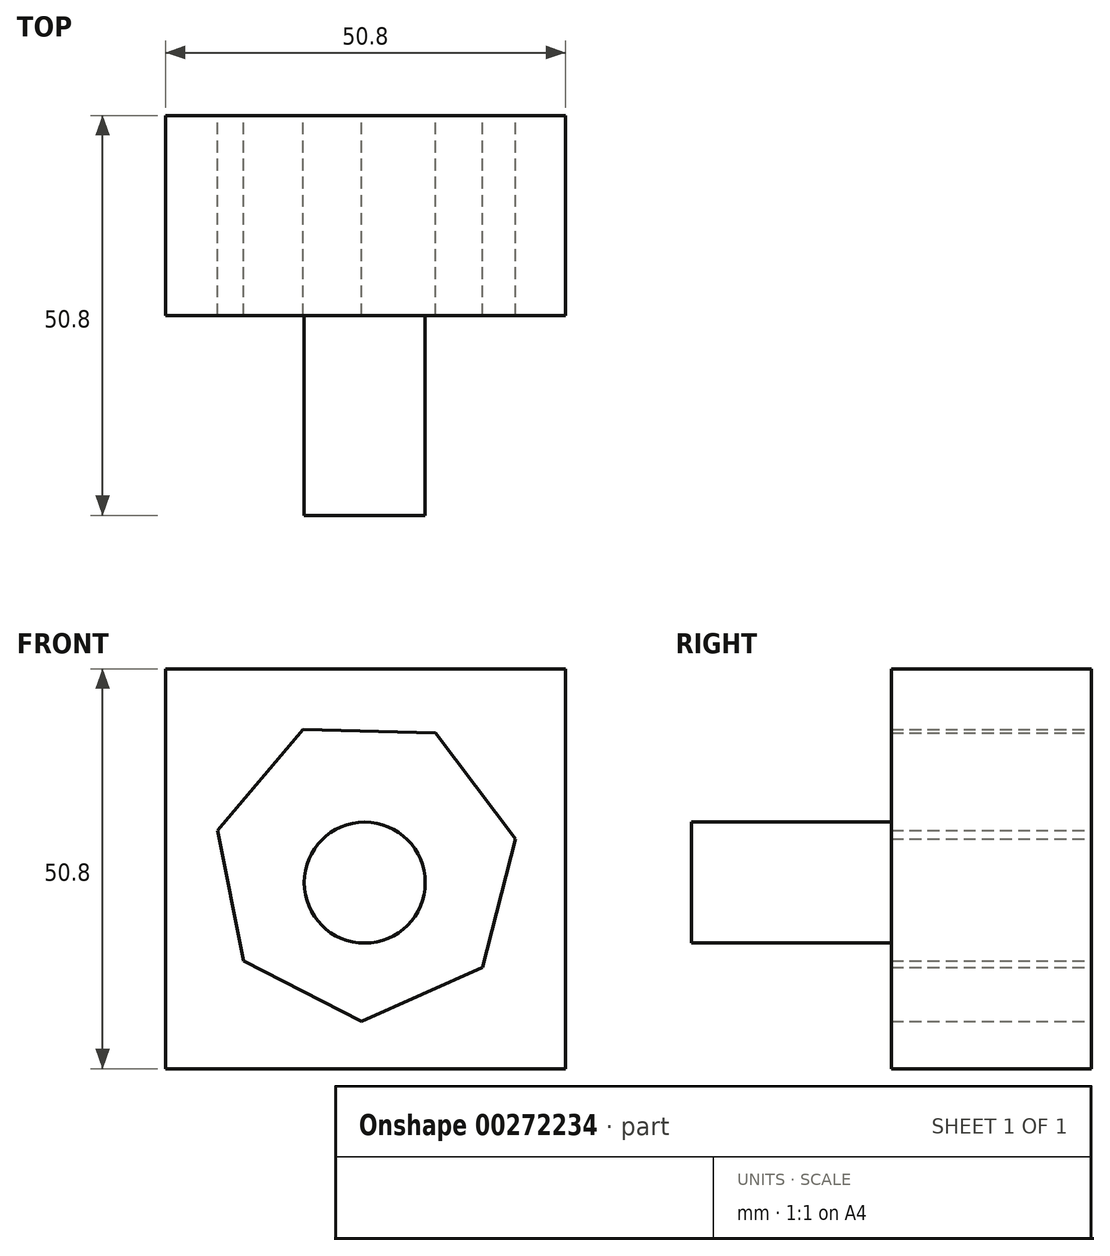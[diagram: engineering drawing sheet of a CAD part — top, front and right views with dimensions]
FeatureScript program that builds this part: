
annotation { "Feature Type Name" : "Feature", "Feature Type Description" : "" }
export const myFeature = defineFeature(function(context is Context, id is Id, definition is map)
    precondition{}
    {
        {
            var Q0;
            Q0=qCreatedBy(makeId("Front.planeOp"),FACE);
            var sketch = newSketch(context, id + "F0", { "sketchPlane" : qUnion([Q0])});
            skLineSegment(sketch, "E0.bottom", {"start": v(-31.05, 34.03) * mm, "end": v(19.75, 34.03) * mm});
            skLineSegment(sketch, "E0.top", {"start": v(-31.05, -16.77) * mm, "end": v(19.75, -16.77) * mm});
            skLineSegment(sketch, "E0.left", {"start": v(-31.05, 34.03) * mm, "end": v(-31.05, -16.77) * mm});
            skLineSegment(sketch, "E0.right", {"start": v(19.75, 34.03) * mm, "end": v(19.75, -16.77) * mm});
            skSolve(sketch);
        }
        {
            var Q0;
            Q0=makeQuery(id+"F0.imprint","IMPRINT",FACE,{"disambiguationData":[TD([[makeQuery(id+"F0.imprint","IMPRINT",EDGE,{"derivedFrom":sQuery(id+"F0.wireOp",EDGE,"E0.bottom")}),-1.0]])]});
            var sketch = newSketch(context, id + "F1", { "sketchPlane" : qUnion([Q0])});
            skCircle(sketch, "E1.cCircle", {"center": v(-5.65, 8.63) * mm, "radius": 17.5 * mm, "construction": true});
            skLineSegment(sketch, "E1.0", {"start": v(3.24, 25.88) * mm, "end": v(13.39, 12.43) * mm});
            skLineSegment(sketch, "E1.1", {"start": v(13.39, 12.43) * mm, "end": v(9.2, -3.88) * mm});
            skLineSegment(sketch, "E1.2", {"start": v(9.2, -3.88) * mm, "end": v(-6.18, -10.78) * mm});
            skLineSegment(sketch, "E1.3", {"start": v(-6.18, -10.78) * mm, "end": v(-21.15, -3.06) * mm});
            skLineSegment(sketch, "E1.4", {"start": v(-21.15, -3.06) * mm, "end": v(-24.45, 13.46) * mm});
            skLineSegment(sketch, "E1.5", {"start": v(-24.45, 13.46) * mm, "end": v(-13.6, 26.34) * mm});
            skLineSegment(sketch, "E1.6", {"start": v(-13.6, 26.34) * mm, "end": v(3.24, 25.88) * mm});
            skPoint(sketch, "E1.0.midPoint", {"position": v(8.31, 19.16) * mm});
            skSolve(sketch);
        }
        {
            var Q0;
            Q0 = qSketchRegion(id + "F1", true);
            var Q1;
            Q1=makeQuery(id+"F0.imprint","IMPRINT",FACE,{"disambiguationData":[TD([[makeQuery(id+"F0.imprint","IMPRINT",EDGE,{"derivedFrom":sQuery(id+"F0.wireOp",EDGE,"E0.bottom")}),-1.0]])]});
            var Q2;
            Q2=makeQuery(id+"F1.imprint","IMPRINT",FACE,{"disambiguationData":[TD([[makeQuery(id+"F1.imprint","IMPRINT",EDGE,{"derivedFrom":sQuery(id+"F1.wireOp",EDGE,"E1.0")}),1.0]])]});
            extrude(context, id + "F2", {"entities" : qUnion([Q0, Q1, Q2]), "depth" : 25.4 * mm});
        }
        {
            var Q0;
            Q0 = qSketchRegion(id + "F1", true);
            extrude(context, id + "F3", {"entities" : qUnion([Q0]), "depth" : 25.4 * mm});
        }
        {
            var Q0;
            {var subQ0=sQuery(id+"F0.wireOp",EDGE,"E0.right");var subQ1=sQuery(id+"F0.wireOp",EDGE,"E0.left");var subQ2=sQuery(id+"F0.wireOp",EDGE,"E0.top");var subQ3=sQuery(id+"F0.wireOp",EDGE,"E0.bottom");Q0=makeQuery(id+"F2.opExtrude","CAP_FACE",FACE,{"disambiguationData":[OSD([subQ3,subQ2,subQ1,subQ0]),TDD([makeQuery(id+"F0.imprint","IMPRINT",EDGE,{"derivedFrom":subQ3}),makeQuery(id+"F0.imprint","IMPRINT",EDGE,{"derivedFrom":subQ2}),makeQuery(id+"F0.imprint","IMPRINT",EDGE,{"derivedFrom":subQ1}),makeQuery(id+"F0.imprint","IMPRINT",EDGE,{"derivedFrom":subQ0})])],"isStart":false});}
            var sketch = newSketch(context, id + "F4", { "sketchPlane" : qUnion([Q0])});
            skCircle(sketch, "E2", {"center": v(-5.76, 6.87) * mm, "radius": 7.7 * mm});
            skSolve(sketch);
        }
        {
            var Q0;
            Q0 = qSketchRegion(id + "F4", true);
            extrude(context, id + "F5", {"entities" : qUnion([Q0]), "depth" : 25.4 * mm});
        }
    });
